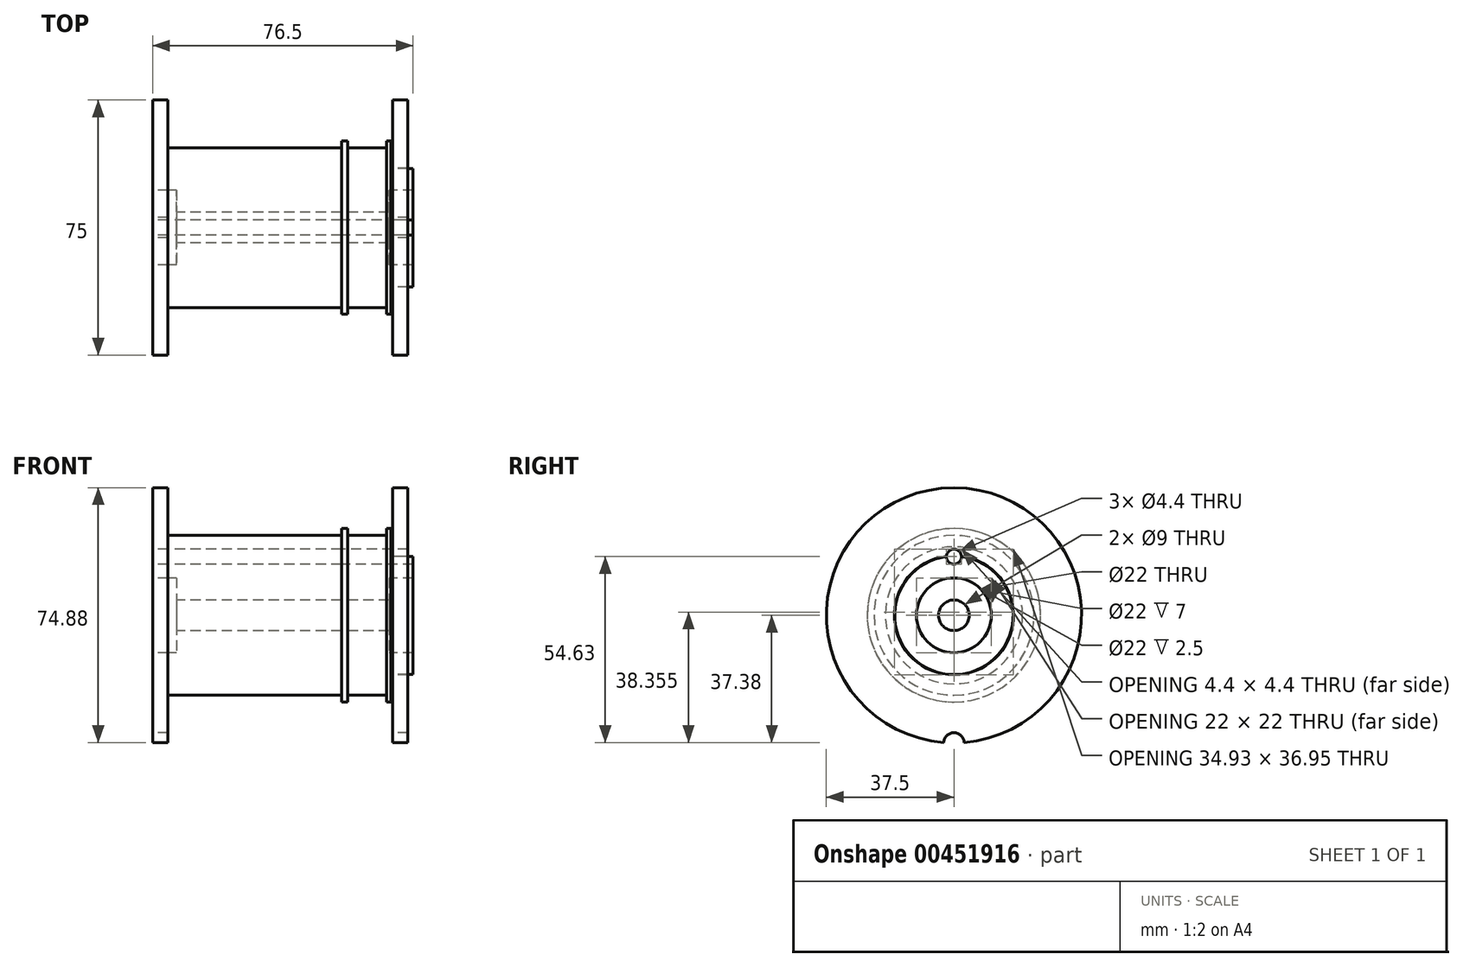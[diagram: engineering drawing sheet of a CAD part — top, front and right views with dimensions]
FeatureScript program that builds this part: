
annotation { "Feature Type Name" : "Feature", "Feature Type Description" : "" }
export const myFeature = defineFeature(function(context is Context, id is Id, definition is map)
    precondition{}
    {
        {
            var Q0;
            Q0=qCreatedBy(makeId("Front.planeOp"),FACE);
            var sketch = newSketch(context, id + "F0", { "sketchPlane" : qUnion([Q0])});
            skLineSegment(sketch, "E0", {"start": v(-32.75, 0) * mm, "end": v(34.5, 0) * mm, "construction": true});
            skLineSegment(sketch, "E1", {"start": v(6.5, 4.5) * mm, "end": v(-7.5, 4.5) * mm});
            skLineSegment(sketch, "E2", {"start": v(-7.5, 11.15) * mm, "end": v(-7.5, 25.5) * mm});
            skLineSegment(sketch, "E3", {"start": v(-7.5, 25.5) * mm, "end": v(-5.75, 25.5) * mm});
            skLineSegment(sketch, "E4", {"start": v(-5.75, 25.5) * mm, "end": v(-5.75, 23.5) * mm});
            skLineSegment(sketch, "E5", {"start": v(-5.75, 23.5) * mm, "end": v(5.75, 23.5) * mm});
            skLineSegment(sketch, "E6", {"start": v(5.75, 23.5) * mm, "end": v(5.75, 25.5) * mm});
            skLineSegment(sketch, "E7", {"start": v(5.75, 25.5) * mm, "end": v(7.5, 25.5) * mm});
            skLineSegment(sketch, "E8", {"start": v(7.5, 25.5) * mm, "end": v(7.5, 17.4) * mm});
            skLineSegment(sketch, "E9", {"start": v(7.5, 17.4) * mm, "end": v(13.5, 17.4) * mm});
            skLineSegment(sketch, "E10", {"start": v(13.5, 17.4) * mm, "end": v(13.5, 11) * mm});
            skLineSegment(sketch, "E11", {"start": v(-7.5, 4.5) * mm, "end": v(-7.5, 11.15) * mm});
            skLineSegment(sketch, "E12", {"start": v(-7.5, 11.15) * mm, "end": v(-7.5, 11.15) * mm});
            skPoint(sketch, "E13", {"position": v(0, 23.5) * mm});
            skLineSegment(sketch, "E14", {"start": v(6.5, 4.5) * mm, "end": v(6.5, 11) * mm});
            skLineSegment(sketch, "E15", {"start": v(6.5, 11) * mm, "end": v(13.5, 11) * mm});
            skPoint(sketch, "E16.orphan", {"position": v(13.5, 4.5) * mm});
            skSolve(sketch);
        }
        {
            var Q0;
            Q0=qSketchRegion(id+"F0",true);
            var Q1;
            Q1=sQuery(id+"F0.wireOp",EDGE,"E0");
            revolve(context, id + "F1", {"entities" : qUnion([Q0]), "axis" : qUnion([Q1]), "revolveType" : RevolveType.FULL});
        }
        {
            var Q0;
            Q0=makeQuery(id+"F1.opRevolve","SWEPT_FACE",FACE,{"disambiguationData":[OSD([sQuery(id+"F0.wireOp",EDGE,"E2")])]});
            var sketch = newSketch(context, id + "F2", { "sketchPlane" : qUnion([Q0])});
            skPoint(sketch, "E17", {"position": v(0, 18.8) * mm});
            skSolve(sketch);
        }
        {
            var Q0;
            Q0=makeQuery(id+"F1.opRevolve","SWEPT_FACE",FACE,{"disambiguationData":[OSD([sQuery(id+"F0.wireOp",EDGE,"E8")])]});
            var sketch = newSketch(context, id + "F3", { "sketchPlane" : qUnion([Q0])});
            skCircle(sketch, "E18", {"center": v(0, 0) * mm, "radius": 20.17 * mm});
            skCircle(sketch, "E19", {"center": v(0, 0) * mm, "radius": 33.41 * mm});
            skSolve(sketch);
        }
        {
            var Q0;
            Q0 = qSketchRegion(id + "F3", true);
            extrude(context, id + "F4", {"entities" : qUnion([Q0]), "operationType" : NewBodyOperationType.REMOVE, "oppositeDirection" : true, "depth" : .5 * mm});
        }
        {
            var Q0;
            Q0=makeQuery(id+"F1.opRevolve","SWEPT_FACE",FACE,{"disambiguationData":[OSD([sQuery(id+"F0.wireOp",EDGE,"E8")])]});
            var sketch = newSketch(context, id + "F5", { "sketchPlane" : qUnion([Q0])});
            skCircle(sketch, "E20", {"center": v(0, 0) * mm, "radius": 37.5 * mm});
            skCircle(sketch, "E21", {"center": v(0, 0) * mm, "radius": 17.5 * mm});
            skSolve(sketch);
        }
        {
            var Q0;
            Q0 = qSketchRegion(id + "F5", true);
            extrude(context, id + "F6", {"entities" : qUnion([Q0]), "depth" : 4.5 * mm, "offsetDistance" : 25 * mm});
        }
        {
            var Q0;
            Q0=makeQuery(id+"F6.opExtrude","CAP_FACE",FACE,{"disambiguationData":[OSD([sQuery(id+"F5.wireOp",EDGE,"E20"),sQuery(id+"F5.wireOp",EDGE,"E21")])],"isStart":false});
            cPlane(context, id + "F7", {"entities" : qUnion([Q0]), "cplaneType" : CPlaneType.OFFSET, "offset" : 75 * mm, "oppositeDirection" : true, "width" : 150 * mm, "height" : 150 * mm});
        }
        {
            var Q0;
            Q0=qCreatedBy(id+"F7.planeOp",FACE);
            var sketch = newSketch(context, id + "F8", { "sketchPlane" : qUnion([Q0])});
            skCircle(sketch, "E22", {"center": v(0, 0) * mm, "radius": 37.5 * mm});
            skCircle(sketch, "E23", {"center": v(0, 0) * mm, "radius": 4.5 * mm});
            skSolve(sketch);
        }
        {
            var Q0;
            Q0 = qSketchRegion(id + "F8", true);
            extrude(context, id + "F9", {"entities" : qUnion([Q0]), "depth" : 4.5 * mm, "offsetDistance" : 25 * mm});
        }
        {
            var Q0;
            Q0=makeQuery(id+"F9.opExtrude","CAP_FACE",FACE,{"disambiguationData":[OSD([sQuery(id+"F8.wireOp",EDGE,"E22")])],"isStart":false});
            var sketch = newSketch(context, id + "F10", { "sketchPlane" : qUnion([Q0])});
            skCircle(sketch, "E24", {"center": v(0, 0) * mm, "radius": 23.5 * mm});
            skCircle(sketch, "E25", {"center": v(0, 0) * mm, "radius": 4.5 * mm});
            skSolve(sketch);
        }
        {
            var Q0;
            Q0 = qSketchRegion(id + "F10", true);
            var Q1;
            Q1=makeQuery(id+"F1.opRevolve","SWEPT_FACE",FACE,{"disambiguationData":[OSD([sQuery(id+"F0.wireOp",EDGE,"E2")])]});
            var Q2;
            Q2=makeQuery(id+"F1.opRevolve","SWEPT_BODY",BODY,{"disambiguationData":[OSD([sQuery(id+"F0.wireOp",EDGE,"E1"),sQuery(id+"F0.wireOp",EDGE,"E2"),sQuery(id+"F0.wireOp",EDGE,"E3"),sQuery(id+"F0.wireOp",EDGE,"E4"),sQuery(id+"F0.wireOp",EDGE,"E5"),sQuery(id+"F0.wireOp",EDGE,"E6"),sQuery(id+"F0.wireOp",EDGE,"E7"),sQuery(id+"F0.wireOp",EDGE,"E8"),sQuery(id+"F0.wireOp",EDGE,"E9"),sQuery(id+"F0.wireOp",EDGE,"E10"),sQuery(id+"F0.wireOp",EDGE,"E11"),sQuery(id+"F0.wireOp",EDGE,"E12")])]});
            extrude(context, id + "F11", {"entities" : qUnion([Q0]), "endBound" : BoundingType.UP_TO_SURFACE, "depth" : 25 * mm, "endBoundEntityFace" : qUnion([Q1]), "endBoundEntityBody" : qUnion([Q2]), "offsetDistance" : 25 * mm});
        }
        {
            var Q0;
            Q0=makeQuery(id+"F9.opExtrude","CAP_FACE",FACE,{"disambiguationData":[OSD([sQuery(id+"F8.wireOp",EDGE,"E22"),sQuery(id+"F8.wireOp",EDGE,"E23")])],"isStart":true});
            var sketch = newSketch(context, id + "F12", { "sketchPlane" : qUnion([Q0])});
            skCircle(sketch, "E26", {"center": v(0, 0) * mm, "radius": 11 * mm});
            skCircle(sketch, "E27.0", {"center": v(0, 0) * mm, "radius": 23.5 * mm, "construction": true});
            skLineSegment(sketch, "E28", {"start": v(0, 11) * mm, "end": v(0, 23.5) * mm, "construction": true});
            skPoint(sketch, "E29", {"position": v(0, 17.25) * mm});
            skSolve(sketch);
        }
        {
            var Q0;
            Q0 = qSketchRegion(id + "F12", true);
            extrude(context, id + "F13", {"entities" : qUnion([Q0]), "operationType" : NewBodyOperationType.REMOVE, "oppositeDirection" : true, "depth" : 7 * mm, "offsetDistance" : 25 * mm});
        }
        {
            var Q0;
            Q0=sQuery(id+"F12.wireOp",VERTEX,"E29");
            var Q1;
            Q1=makeQuery(id+"F9.opExtrude","SWEPT_BODY",BODY,{"disambiguationData":[OSD([sQuery(id+"F8.wireOp",EDGE,"E22"),sQuery(id+"F8.wireOp",EDGE,"E23")])]});
            var Q2;
            Q2=makeQuery(id+"F11.opExtrude","SWEPT_BODY",BODY,{"disambiguationData":[OSD([sQuery(id+"F10.wireOp",EDGE,"E24"),sQuery(id+"F10.wireOp",EDGE,"E25")])]});
            var Q3;
            Q3=makeQuery(id+"F1.opRevolve","SWEPT_BODY",BODY,{"disambiguationData":[OSD([sQuery(id+"F0.wireOp",EDGE,"E1"),sQuery(id+"F0.wireOp",EDGE,"E2"),sQuery(id+"F0.wireOp",EDGE,"E3"),sQuery(id+"F0.wireOp",EDGE,"E4"),sQuery(id+"F0.wireOp",EDGE,"E5"),sQuery(id+"F0.wireOp",EDGE,"E6"),sQuery(id+"F0.wireOp",EDGE,"E7"),sQuery(id+"F0.wireOp",EDGE,"E8"),sQuery(id+"F0.wireOp",EDGE,"E9"),sQuery(id+"F0.wireOp",EDGE,"E10"),sQuery(id+"F0.wireOp",EDGE,"E11")])]});
            var Q4;
            Q4=makeQuery(id+"F6.opExtrude","SWEPT_BODY",BODY,{"disambiguationData":[OSD([sQuery(id+"F5.wireOp",EDGE,"E20"),sQuery(id+"F5.wireOp",EDGE,"E21")])]});
            hole(context, id + "F14", {"style" : HoleStyle.SIMPLE, "endStyle" : HoleEndStyle.THROUGH, "standardTappedOrClearance" : lookupTablePath({ "standard" : "ISO", "fit" : "Normal", "size" : "M4", "type" : "Clearance" }), "standardBlindInLast" : lookupTablePath({ "fit" : "Standard", "standard" : "ISO", "size" : "M4", "type" : "Clearance" }), "holeDiameter" : 4.4 * mm, "tappedDepth" : 12 * mm, "tapClearance" : 3, "locations" : qUnion([Q0]), "scope" : qUnion([Q1, Q2, Q3, Q4])});
        }
        {
            var Q0;
            Q0=makeQuery(id+"F9.opExtrude","CAP_FACE",FACE,{"disambiguationData":[OSD([sQuery(id+"F8.wireOp",EDGE,"E22"),sQuery(id+"F8.wireOp",EDGE,"E23")])],"isStart":true});
            var sketch = newSketch(context, id + "F15", { "sketchPlane" : qUnion([Q0])});
            skCircle(sketch, "E30", {"center": v(0, -37.5) * mm, "radius": 3 * mm});
            skSolve(sketch);
        }
        {
            var Q0;
            Q0 = qSketchRegion(id + "F15", true);
            extrude(context, id + "F16", {"entities" : qUnion([Q0]), "operationType" : NewBodyOperationType.REMOVE, "endBound" : BoundingType.THROUGH_ALL, "oppositeDirection" : true, "depth" : 25 * mm, "offsetDistance" : 25 * mm});
        }
    });
